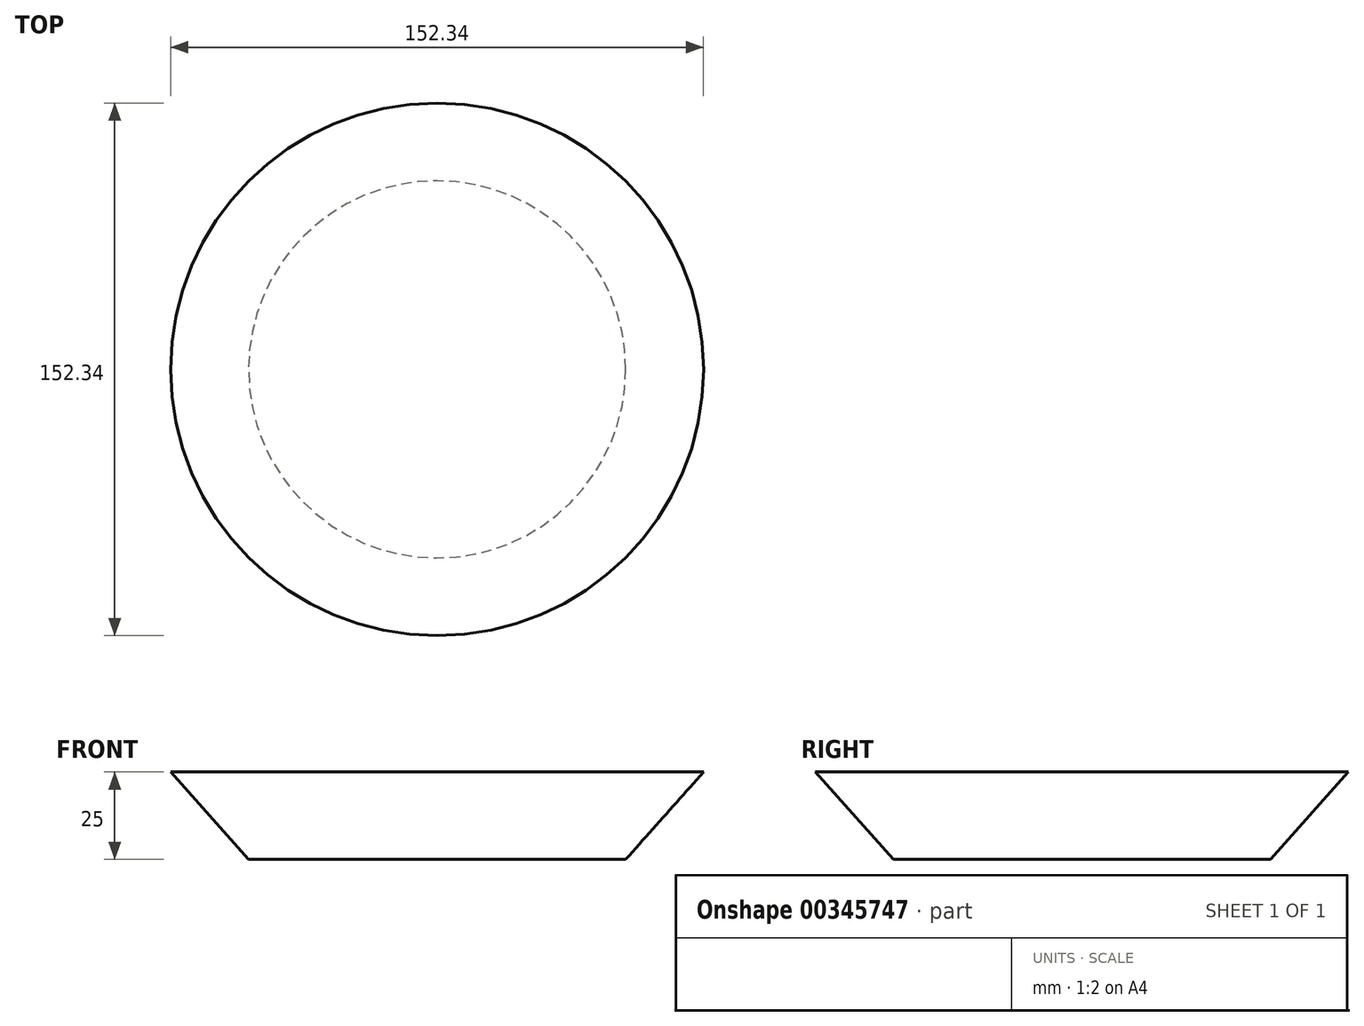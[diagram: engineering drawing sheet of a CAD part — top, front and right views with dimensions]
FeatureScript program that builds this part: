
annotation { "Feature Type Name" : "Feature", "Feature Type Description" : "" }
export const myFeature = defineFeature(function(context is Context, id is Id, definition is map)
    precondition{}
    {
        {
            var Q0;
            Q0=qCreatedBy(makeId("Top.planeOp"),FACE);
            var sketch = newSketch(context, id + "F0", { "sketchPlane" : qUnion([Q0])});
            skCircle(sketch, "E0", {"center": v(0, 0) * mm, "radius": 53.92 * mm});
            skSolve(sketch);
        }
        {
            var Q0;
            Q0=qCreatedBy(makeId("Top.planeOp"),FACE);
            cPlane(context, id + "F1", {"entities" : qUnion([Q0]), "cplaneType" : CPlaneType.OFFSET, "offset" : 25 * mm, "width" : 152.4 * mm, "height" : 152.4 * mm});
        }
        {
            var Q0;
            Q0=qCreatedBy(id+"F1.planeOp",FACE);
            var sketch = newSketch(context, id + "F2", { "sketchPlane" : qUnion([Q0])});
            skCircle(sketch, "E1", {"center": v(0, 0) * mm, "radius": 76.17 * mm});
            skSolve(sketch);
        }
        {
            var Q0;
            Q0=makeQuery(id+"F0.imprint","IMPRINT",FACE,{"disambiguationData":[TD([[makeQuery(id+"F0.imprint","IMPRINT",EDGE,{"derivedFrom":sQuery(id+"F0.wireOp",EDGE,"E0")}),1.0]])]});
            var Q1;
            Q1=makeQuery(id+"F2.imprint","IMPRINT",FACE,{"disambiguationData":[TD([[makeQuery(id+"F2.imprint","IMPRINT",EDGE,{"derivedFrom":sQuery(id+"F2.wireOp",EDGE,"E1")}),1.0]])]});
            loft(context, id + "F3", {"sheetProfilesArray" : [{ "sheetProfileEntities" : qUnion([Q0]) }, { "sheetProfileEntities" : qUnion([Q1]) }]});
        }
    });
